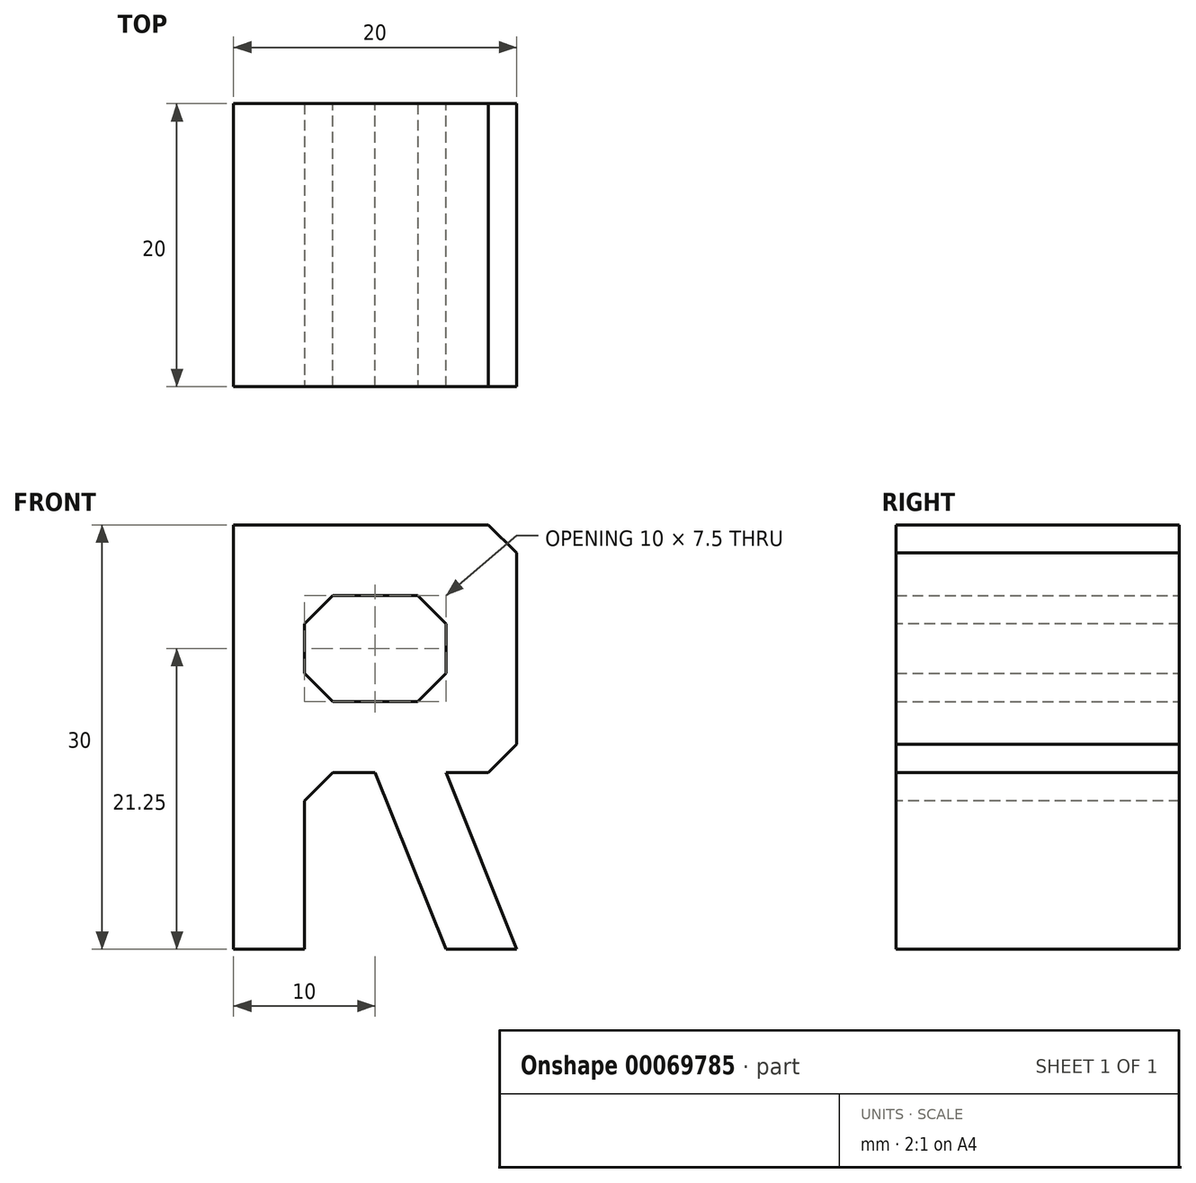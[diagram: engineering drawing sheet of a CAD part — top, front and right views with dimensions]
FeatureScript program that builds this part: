
annotation { "Feature Type Name" : "Feature", "Feature Type Description" : "" }
export const myFeature = defineFeature(function(context is Context, id is Id, definition is map)
    precondition{}
    {
        {
            var Q0;
            Q0=qCreatedBy(makeId("Front.planeOp"),FACE);
            var sketch = newSketch(context, id + "F0", { "sketchPlane" : qUnion([Q0])});
            skLineSegment(sketch, "E0.bottom", {"start": v(0, 0) * mm, "end": v(5, 0) * mm});
            skLineSegment(sketch, "E0.top", {"start": v(0, 30) * mm, "end": v(20, 30) * mm});
            skLineSegment(sketch, "E0.left", {"start": v(0, 0) * mm, "end": v(0, 30) * mm});
            skLineSegment(sketch, "E1", {"start": v(5, 25) * mm, "end": v(5, 17.5) * mm});
            skLineSegment(sketch, "E2", {"start": v(15, 25) * mm, "end": v(15, 17.5) * mm});
            skLineSegment(sketch, "E3", {"start": v(5, 25) * mm, "end": v(15, 25) * mm});
            skLineSegment(sketch, "E4", {"start": v(20, 0) * mm, "end": v(15, 0) * mm});
            skLineSegment(sketch, "E5", {"start": v(5, 17.5) * mm, "end": v(15, 17.5) * mm});
            skLineSegment(sketch, "E6", {"start": v(20, 30) * mm, "end": v(20, 12.5) * mm});
            skPoint(sketch, "E7.start.orphan", {"position": v(0, 15) * mm});
            skLineSegment(sketch, "E8.trimOffspring", {"start": v(5, 12.5) * mm, "end": v(5, 0) * mm});
            skLineSegment(sketch, "E9", {"start": v(20, 0) * mm, "end": v(15, 12.5) * mm});
            skLineSegment(sketch, "E10", {"start": v(5, 12.5) * mm, "end": v(10, 12.5) * mm});
            skLineSegment(sketch, "E11", {"start": v(10, 12.5) * mm, "end": v(15, 0) * mm});
            skLineSegment(sketch, "E12", {"start": v(15, 12.5) * mm, "end": v(20, 12.5) * mm});
            skLineSegment(sketch, "E13.trimOffspring", {"start": v(15, 0) * mm, "end": v(20, 0) * mm});
            skSolve(sketch);
        }
        {
            var Q0;
            Q0=makeQuery(id+"F0.imprint","IMPRINT",FACE,{"disambiguationData":[TD([[makeQuery(id+"F0.imprint","IMPRINT",EDGE,{"derivedFrom":sQuery(id+"F0.wireOp",EDGE,"E0.bottom")}),1.0]])]});
            extrude(context, id + "F1", {"entities" : qUnion([Q0]), "depth" : 20 * mm});
        }
        {
            var Q0;
            Q0=makeQuery(id+"F1.opExtrude","SWEPT_EDGE",EDGE,{"disambiguationData":[OSD([sQuery(id+"F0.wireOp",EDGE,"E0.top"),sQuery(id+"F0.wireOp",EDGE,"E6")])]});
            var Q1;
            Q1=makeQuery(id+"F1.opExtrude","SWEPT_EDGE",EDGE,{"disambiguationData":[OSD([sQuery(id+"F0.wireOp",EDGE,"E6"),sQuery(id+"F0.wireOp",EDGE,"E12")])]});
            var Q2;
            Q2=makeQuery(id+"F1.opExtrude","SWEPT_EDGE",EDGE,{"disambiguationData":[OSD([sQuery(id+"F0.wireOp",EDGE,"E1"),sQuery(id+"F0.wireOp",EDGE,"E5")])]});
            var Q3;
            Q3=makeQuery(id+"F1.opExtrude","SWEPT_EDGE",EDGE,{"disambiguationData":[OSD([sQuery(id+"F0.wireOp",EDGE,"E1"),sQuery(id+"F0.wireOp",EDGE,"E3")])]});
            var Q4;
            Q4=makeQuery(id+"F1.opExtrude","SWEPT_EDGE",EDGE,{"disambiguationData":[OSD([sQuery(id+"F0.wireOp",EDGE,"E8.trimOffspring"),sQuery(id+"F0.wireOp",EDGE,"E10")])]});
            var Q5;
            Q5=makeQuery(id+"F1.opExtrude","SWEPT_EDGE",EDGE,{"disambiguationData":[OSD([sQuery(id+"F0.wireOp",EDGE,"E2"),sQuery(id+"F0.wireOp",EDGE,"E3")])]});
            var Q6;
            Q6=makeQuery(id+"F1.opExtrude","SWEPT_EDGE",EDGE,{"disambiguationData":[OSD([sQuery(id+"F0.wireOp",EDGE,"E2"),sQuery(id+"F0.wireOp",EDGE,"E5")])]});
            chamfer(context, id + "F2", {"entities" : qUnion([Q0, Q1, Q2, Q3, Q4, Q5, Q6]), "width" : 2 * mm, "tangentPropagation" : true});
        }
    });
